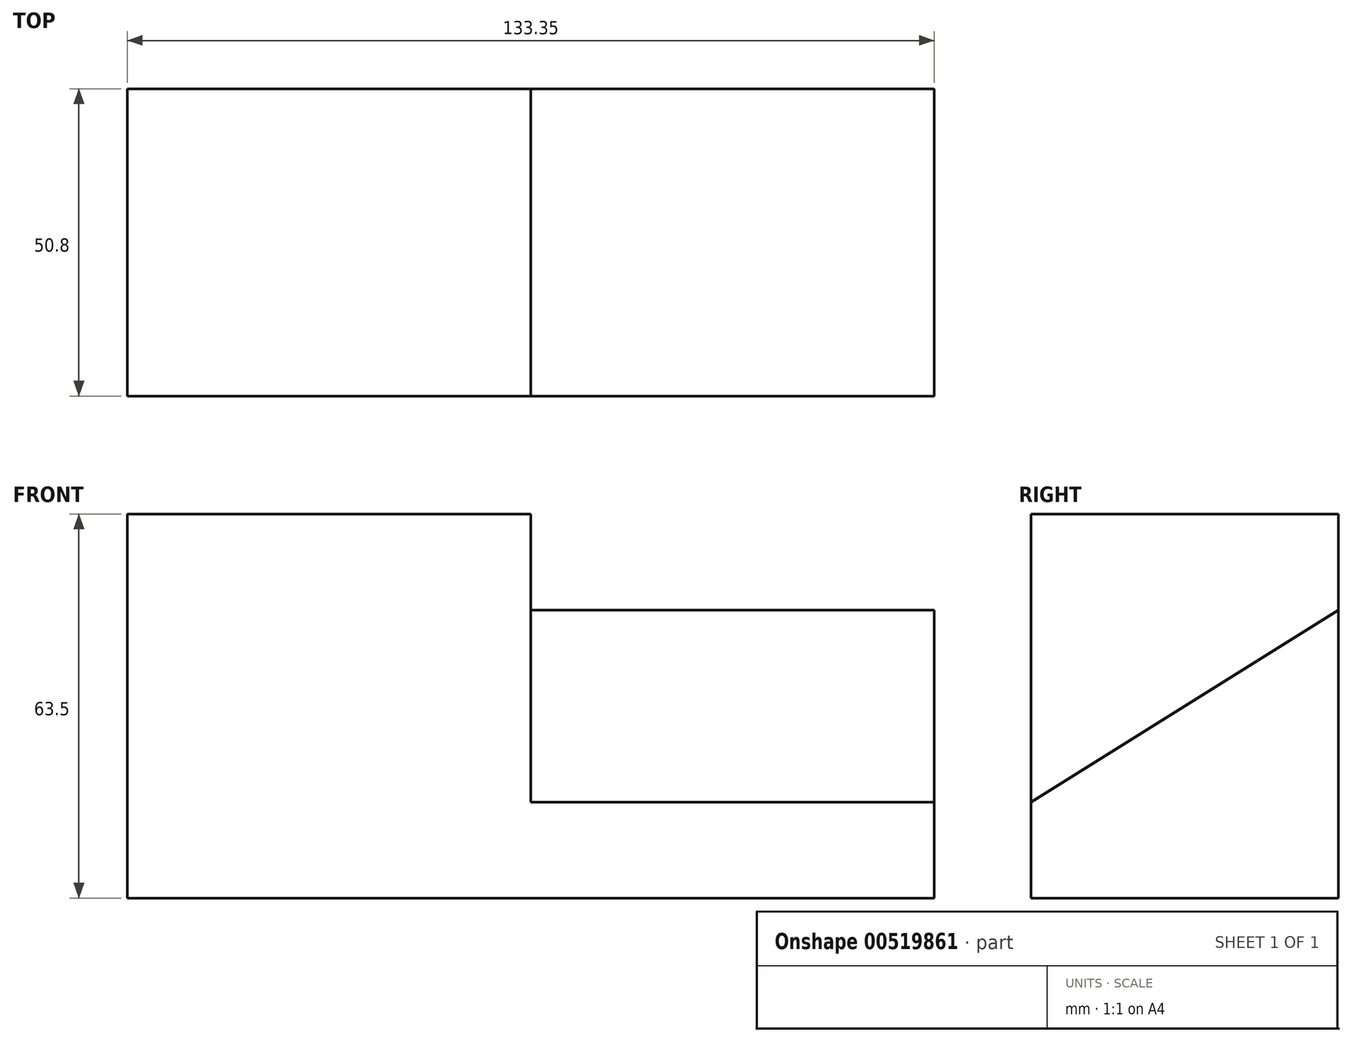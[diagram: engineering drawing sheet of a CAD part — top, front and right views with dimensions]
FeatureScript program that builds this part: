
annotation { "Feature Type Name" : "Feature", "Feature Type Description" : "" }
export const myFeature = defineFeature(function(context is Context, id is Id, definition is map)
    precondition{}
    {
        {
            var Q0;
            Q0=qCreatedBy(makeId("Front.planeOp"),FACE);
            var sketch = newSketch(context, id + "F0", { "sketchPlane" : qUnion([Q0])});
            skLineSegment(sketch, "E0", {"start": v(-65.25, -39.19) * mm, "end": v(68.1, -39.19) * mm});
            skLineSegment(sketch, "E1", {"start": v(-65.25, -39.19) * mm, "end": v(-65.25, 24.31) * mm});
            skLineSegment(sketch, "E2", {"start": v(-65.25, 24.31) * mm, "end": v(68.1, 24.31) * mm});
            skLineSegment(sketch, "E3", {"start": v(68.1, 24.31) * mm, "end": v(68.1, -39.19) * mm});
            skSolve(sketch);
        }
        {
            var Q0;
            Q0=makeQuery(id+"F0.imprint","IMPRINT",FACE,{"disambiguationData":[TD([[makeQuery(id+"F0.imprint","IMPRINT",EDGE,{"derivedFrom":sQuery(id+"F0.wireOp",EDGE,"E0")}),1.0]])]});
            extrude(context, id + "F1", {"entities" : qUnion([Q0]), "depth" : 50.8 * mm, "offsetDistance" : 25.4 * mm});
        }
        {
            var Q0;
            Q0=makeQuery(id+"F1.opExtrude","SWEPT_FACE",FACE,{"disambiguationData":[OSD([sQuery(id+"F0.wireOp",EDGE,"E3")])]});
            var sketch = newSketch(context, id + "F2", { "sketchPlane" : qUnion([Q0])});
            skLineSegment(sketch, "E4", {"start": v(-50.8, -39.19) * mm, "end": v(-50.8, -23.31) * mm});
            skLineSegment(sketch, "E5", {"start": v(0, 24.31) * mm, "end": v(0, 8.44) * mm});
            skLineSegment(sketch, "E6", {"start": v(-50.8, -23.31) * mm, "end": v(0, 8.44) * mm});
            skSolve(sketch);
        }
        {
            var Q0;
            Q0=makeQuery(id+"F2.imprint","IMPRINT",FACE,{"disambiguationData":[TD([[makeQuery(id+"F2.imprint","IMPRINT",EDGE,{"derivedFrom":sQuery(id+"F2.wireOp",EDGE,"E5")}),-1.0]])]});
            extrude(context, id + "F3", {"entities" : qUnion([Q0]), "operationType" : NewBodyOperationType.REMOVE, "oppositeDirection" : true, "depth" : 66.67 * mm, "offsetDistance" : 25.4 * mm});
        }
    });
